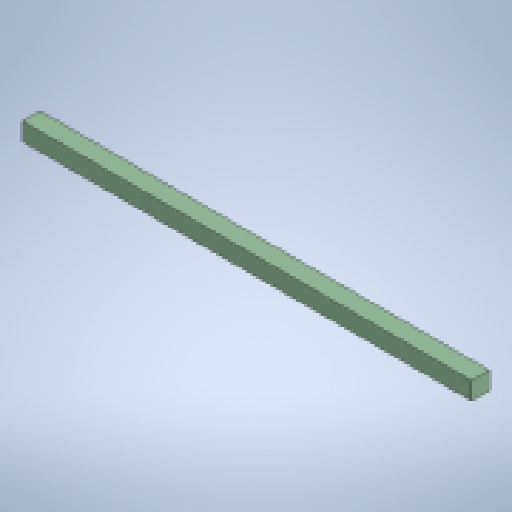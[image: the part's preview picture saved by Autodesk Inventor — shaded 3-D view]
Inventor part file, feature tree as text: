
AUTODESK INVENTOR PART (.ipt)
format: ipt  version: 2025.1 (Build 291241020, 241B)  size: 136,192 bytes
history: native  units: in
note: dims shown in document units (in); Inventor stores cm internally (conversion verified against a paired STEP export)
features: extrude x1, sketch x1, other x1
ambient origin geometry x8: Origin, YZ Plane, XZ Plane, XY Plane, X Axis, Y Axis, Z Axis, Center Point
bodies: Solid1 (feature_tree)
feature tree (3):
  extrude  "Extrusion1"  Depth=3.5in
  sketch  "Sketch1"  dims[d0=3.5in d1=3.5in d2=89.0in d3=0.0in]
  other  "Finish1"
